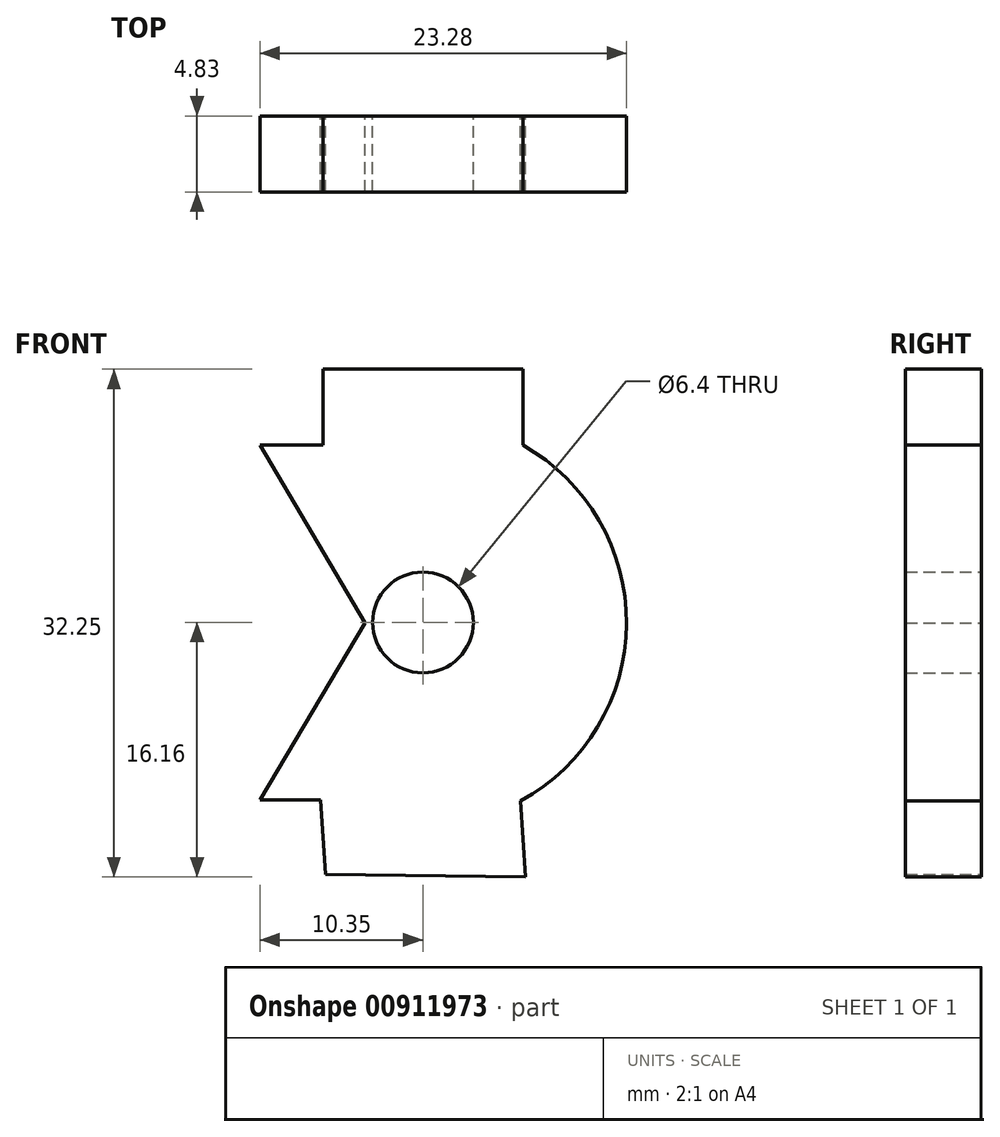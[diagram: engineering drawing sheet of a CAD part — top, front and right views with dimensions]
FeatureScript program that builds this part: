
annotation { "Feature Type Name" : "Feature", "Feature Type Description" : "" }
export const myFeature = defineFeature(function(context is Context, id is Id, definition is map)
    precondition{}
    {
        {
            var Q0;
            Q0=qCreatedBy(makeId("Front.planeOp"),FACE);
            var sketch = newSketch(context, id + "F0", { "sketchPlane" : qUnion([Q0])});
            skLineSegment(sketch, "E0.bottom", {"start": v(6.5, -16.16) * mm, "end": v(-6.2, -16) * mm});
            skLineSegment(sketch, "E0.left", {"start": v(6.5, -16.16) * mm, "end": v(6.2, -11.34) * mm});
            skLineSegment(sketch, "E0.right", {"start": v(-6.2, -16) * mm, "end": v(-6.5, -11.18) * mm});
            skPoint(sketch, "E0.middle", {"position": v(0, -13.67) * mm});
            skArc(sketch, "E1", {"start": v(6.2, -11.34) * mm, "mid": v(12.93, -0.09) * mm, "end": v(6.35, 11.26) * mm});
            skPoint(sketch, "E2.center", {"position": v(0, -0.04) * mm});
            skLineSegment(sketch, "E3.top", {"start": v(6.35, 16.09) * mm, "end": v(-6.35, 16.09) * mm});
            skLineSegment(sketch, "E3.left", {"start": v(6.35, 11.26) * mm, "end": v(6.35, 16.09) * mm});
            skLineSegment(sketch, "E3.right", {"start": v(-6.35, 11.26) * mm, "end": v(-6.35, 16.09) * mm});
            skPoint(sketch, "E3.middle", {"position": v(0, 13.67) * mm});
            skCircle(sketch, "E4", {"center": v(0, 0) * mm, "radius": 3.2 * mm});
            skLineSegment(sketch, "E5.bottom", {"start": v(-6.35, 11.26) * mm, "end": v(-10.35, 11.26) * mm});
            skLineSegment(sketch, "E5.top", {"start": v(-6.35, -11.26) * mm, "end": v(-10.35, -11.26) * mm});
            skLineSegment(sketch, "E5.right", {"start": v(-10.35, 11.26) * mm, "end": v(-10.35, -11.26) * mm});
            skPoint(sketch, "E5.middle", {"position": v(-8.35, 0) * mm});
            skLineSegment(sketch, "E6", {"start": v(-10.35, 11.26) * mm, "end": v(-3.69, -0.04) * mm});
            skLineSegment(sketch, "E7", {"start": v(-3.69, -0.04) * mm, "end": v(-10.35, -11.26) * mm});
            skSolve(sketch);
        }
        {
            var Q0;
            Q0=makeQuery(id+"F0.imprint","IMPRINT",FACE,{"disambiguationData":[TD([[makeQuery(id+"F0.imprint","IMPRINT",EDGE,{"derivedFrom":sQuery(id+"F0.wireOp",EDGE,"E5.bottom")}),1.0]])]});
            var Q1;
            {var subQ1=sQuery(id+"F0.wireOp",EDGE,"E0.bottom");Q1=makeQuery(id+"F0.imprint","IMPRINT",FACE,{"disambiguationData":[TD([[makeQuery(id+"F0.imprint","IMPRINT",EDGE,{"derivedFrom":subQ1}),-1.0]])]});}
            extrude(context, id + "F1", {"entities" : qUnion([Q0, Q1]), "depth" : 4.83 * mm, "offsetDistance" : 25.4 * mm});
        }
    });
